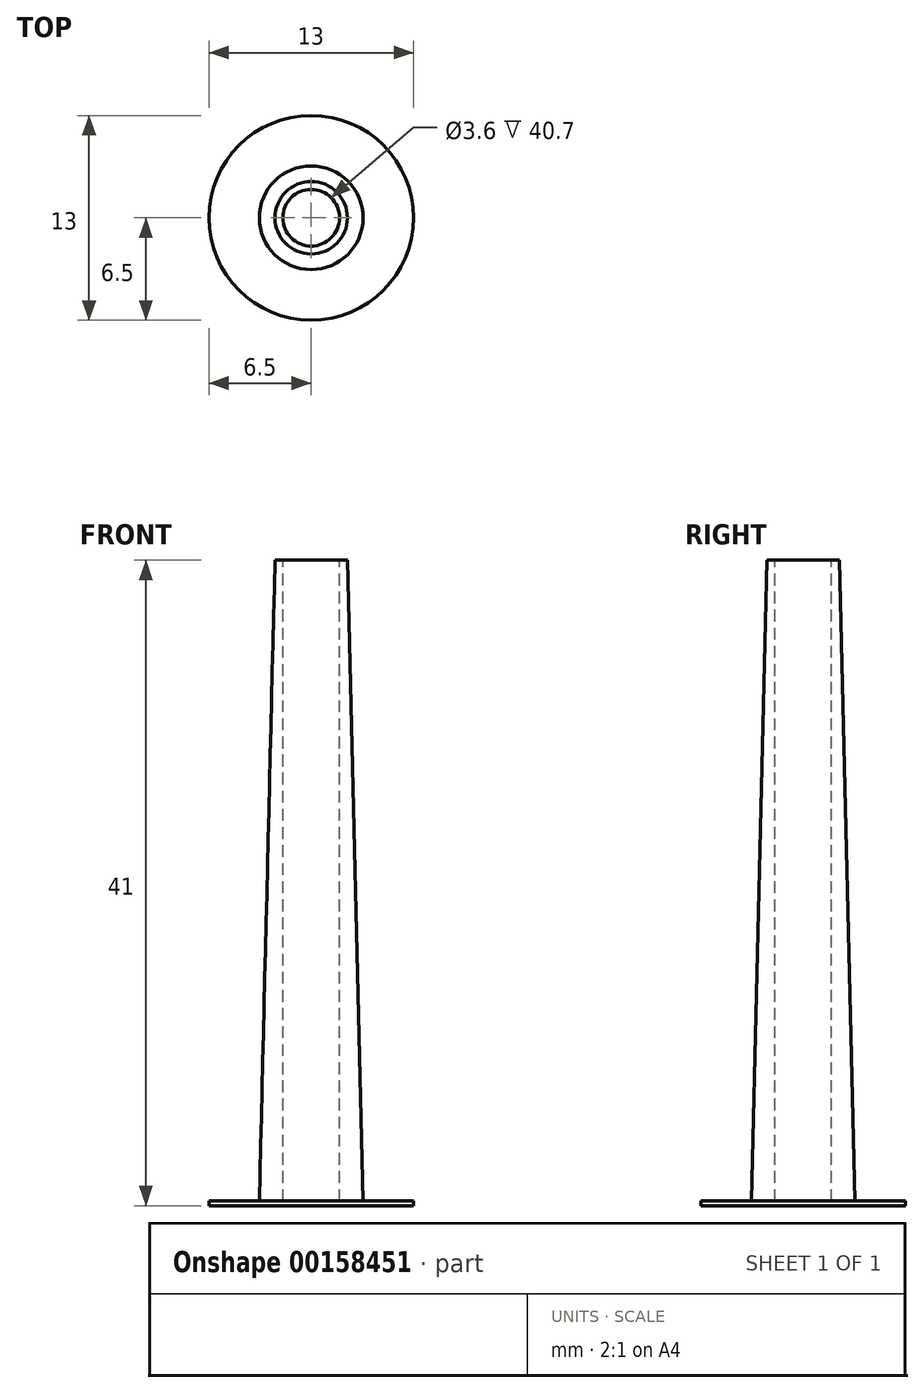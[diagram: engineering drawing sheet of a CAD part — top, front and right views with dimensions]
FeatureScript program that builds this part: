
annotation { "Feature Type Name" : "Feature", "Feature Type Description" : "" }
export const myFeature = defineFeature(function(context is Context, id is Id, definition is map)
    precondition{}
    {
        {
            var Q0;
            Q0=qCreatedBy(makeId("Top.planeOp"),FACE);
            var sketch = newSketch(context, id + "F0", { "sketchPlane" : qUnion([Q0])});
            skCircle(sketch, "E0", {"center": v(0, 0) * mm, "radius": 1.8 * mm, "construction": true});
            skCircle(sketch, "E1.0", {"center": v(0, 0) * mm, "radius": 3.3 * mm});
            skSolve(sketch);
        }
        {
            var Q0;
            Q0=makeQuery(id+"F0.imprint","IMPRINT",FACE,{"disambiguationData":[TD([[makeQuery(id+"F0.imprint","IMPRINT",EDGE,{"derivedFrom":sQuery(id+"F0.wireOp",EDGE,"E1.0")}),1.0]])]});
            cPlane(context, id + "F1", {"entities" : qUnion([Q0]), "cplaneType" : CPlaneType.OFFSET, "offset" : 41 * mm, "width" : 150 * mm, "height" : 150 * mm});
        }
        {
            var Q0;
            Q0=qCreatedBy(id+"F1.planeOp",FACE);
            var sketch = newSketch(context, id + "F2", { "sketchPlane" : qUnion([Q0])});
            skCircle(sketch, "E2.0", {"center": v(0, 0) * mm, "radius": 1.8 * mm, "construction": true});
            skCircle(sketch, "E3.0", {"center": v(0, 0) * mm, "radius": 2.3 * mm});
            skSolve(sketch);
        }
        {
            var Q0;
            Q0=makeQuery(id+"F0.imprint","IMPRINT",FACE,{"disambiguationData":[TD([[makeQuery(id+"F0.imprint","IMPRINT",EDGE,{"derivedFrom":sQuery(id+"F0.wireOp",EDGE,"E1.0")}),1.0]])]});
            var Q1;
            Q1=makeQuery(id+"F2.imprint","IMPRINT",FACE,{"disambiguationData":[TD([[makeQuery(id+"F2.imprint","IMPRINT",EDGE,{"derivedFrom":sQuery(id+"F2.wireOp",EDGE,"E3.0")}),1.0]])]});
            loft(context, id + "F3", {"sheetProfilesArray" : [{ "sheetProfileEntities" : qUnion([Q0]) }, { "sheetProfileEntities" : qUnion([Q1]) }]});
        }
        {
            var Q0;
            Q0=makeQuery(id+"F3.opLoft","CAP_FACE",FACE,{"disambiguationData":[OSD([makeQuery(id+"F2.imprint","IMPRINT",FACE,{"disambiguationData":[TD([[makeQuery(id+"F2.imprint","IMPRINT",EDGE,{"derivedFrom":sQuery(id+"F2.wireOp",EDGE,"E3.0")}),1.0]])]})])],"isStart":true});
            var sketch = newSketch(context, id + "F4", { "sketchPlane" : qUnion([Q0])});
            skCircle(sketch, "E4.0", {"center": v(0, 0) * mm, "radius": 1.8 * mm});
            skSolve(sketch);
        }
        {
            var Q0;
            Q0 = qSketchRegion(id + "F4", true);
            extrude(context, id + "F5", {"entities" : qUnion([Q0]), "operationType" : NewBodyOperationType.REMOVE, "endBound" : BoundingType.THROUGH_ALL, "oppositeDirection" : true, "depth" : 25 * mm});
        }
        {
            var Q0;
            Q0=makeQuery(id+"F3.opLoft","CAP_FACE",FACE,{"disambiguationData":[OSD([makeQuery(id+"F0.imprint","IMPRINT",FACE,{"disambiguationData":[TD([[makeQuery(id+"F0.imprint","IMPRINT",EDGE,{"derivedFrom":sQuery(id+"F0.wireOp",EDGE,"E1.0")}),1.0]])]})])],"isStart":true});
            var sketch = newSketch(context, id + "F6", { "sketchPlane" : qUnion([Q0])});
            skCircle(sketch, "E5", {"center": v(0, 0) * mm, "radius": 6.5 * mm});
            skSolve(sketch);
        }
        {
            var Q0;
            Q0 = qSketchRegion(id + "F6", true);
            extrude(context, id + "F7", {"entities" : qUnion([Q0]), "operationType" : NewBodyOperationType.ADD, "oppositeDirection" : true, "depth" : .3 * mm});
        }
    });
